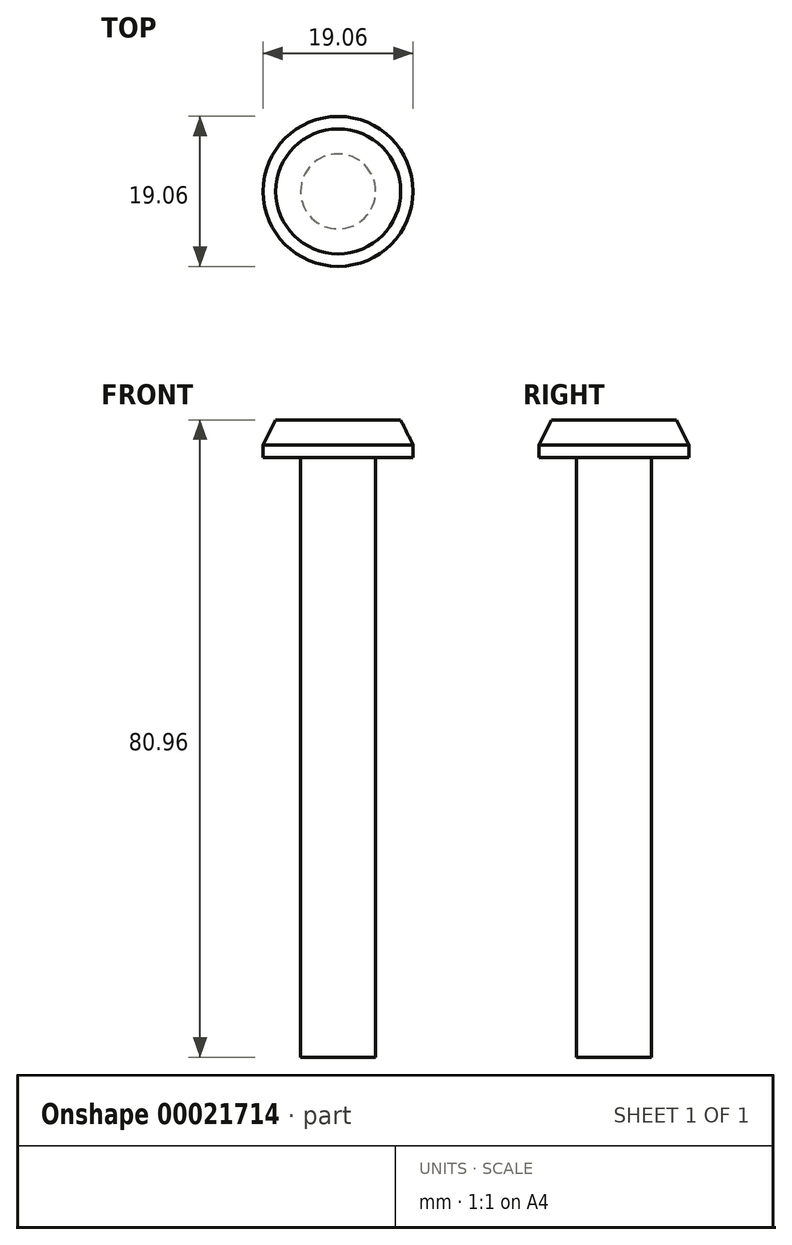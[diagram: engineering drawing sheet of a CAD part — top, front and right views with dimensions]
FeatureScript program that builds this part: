
annotation { "Feature Type Name" : "Feature", "Feature Type Description" : "" }
export const myFeature = defineFeature(function(context is Context, id is Id, definition is map)
    precondition{}
    {
        {
            var Q0;
            Q0=qCreatedBy(makeId("Front.planeOp"),FACE);
            var sketch = newSketch(context, id + "F0", { "sketchPlane" : qUnion([Q0])});
            skLineSegment(sketch, "E0", {"start": v(0, 36.37) * mm, "end": v(0, -39.83) * mm});
            skLineSegment(sketch, "E1", {"start": v(0, 36.37) * mm, "end": v(4.76, 36.37) * mm});
            skLineSegment(sketch, "E2", {"start": v(4.76, 36.37) * mm, "end": v(4.76, -39.83) * mm});
            skLineSegment(sketch, "E3", {"start": v(4.76, -39.83) * mm, "end": v(0, -39.83) * mm});
            skLineSegment(sketch, "E4", {"start": v(0, 36.37) * mm, "end": v(9.53, 36.37) * mm});
            skLineSegment(sketch, "E5", {"start": v(9.53, 36.37) * mm, "end": v(9.53, 37.96) * mm});
            skLineSegment(sketch, "E6", {"start": v(9.53, 37.96) * mm, "end": v(0, 37.96) * mm});
            skLineSegment(sketch, "E7", {"start": v(0, 37.96) * mm, "end": v(0, 36.37) * mm});
            skLineSegment(sketch, "E8", {"start": v(0, 37.96) * mm, "end": v(0, 41.13) * mm});
            skLineSegment(sketch, "E9", {"start": v(0, 39.54) * mm, "end": v(0, 36.37) * mm});
            skLineSegment(sketch, "E10", {"start": v(0, 41.13) * mm, "end": v(7.94, 41.13) * mm});
            skLineSegment(sketch, "E11", {"start": v(9.53, 37.96) * mm, "end": v(7.94, 41.13) * mm});
            skSolve(sketch);
        }
        {
            var Q0;
            {var subQ2=sQuery(id+"F0.wireOp",EDGE,"E6");Q0=makeQuery(id+"F0.imprint","IMPRINT",FACE,{"disambiguationData":[TD([[makeQuery(id+"F0.imprint","IMPRINT",EDGE,{"derivedFrom":subQ2}),-1.0]])]});}
            var Q1;
            {var subQ4=sQuery(id+"F0.wireOp",EDGE,"E5");Q1=makeQuery(id+"F0.imprint","IMPRINT",FACE,{"disambiguationData":[TD([[makeQuery(id+"F0.imprint","IMPRINT",EDGE,{"derivedFrom":subQ4}),1.0]])]});}
            var Q2;
            {var subQ2=sQuery(id+"F0.wireOp",EDGE,"E0");Q2=makeQuery(id+"F0.imprint","IMPRINT",FACE,{"disambiguationData":[TD([[makeQuery(id+"F0.imprint","IMPRINT",EDGE,{"derivedFrom":subQ2}),1.0]])]});}
            var Q3;
            Q3=sQuery(id+"F0.wireOp",EDGE,"E0");
            revolve(context, id + "F1", {"entities" : qUnion([Q0, Q1, Q2]), "axis" : qUnion([Q3]), "revolveType" : RevolveType.FULL});
        }
    });
